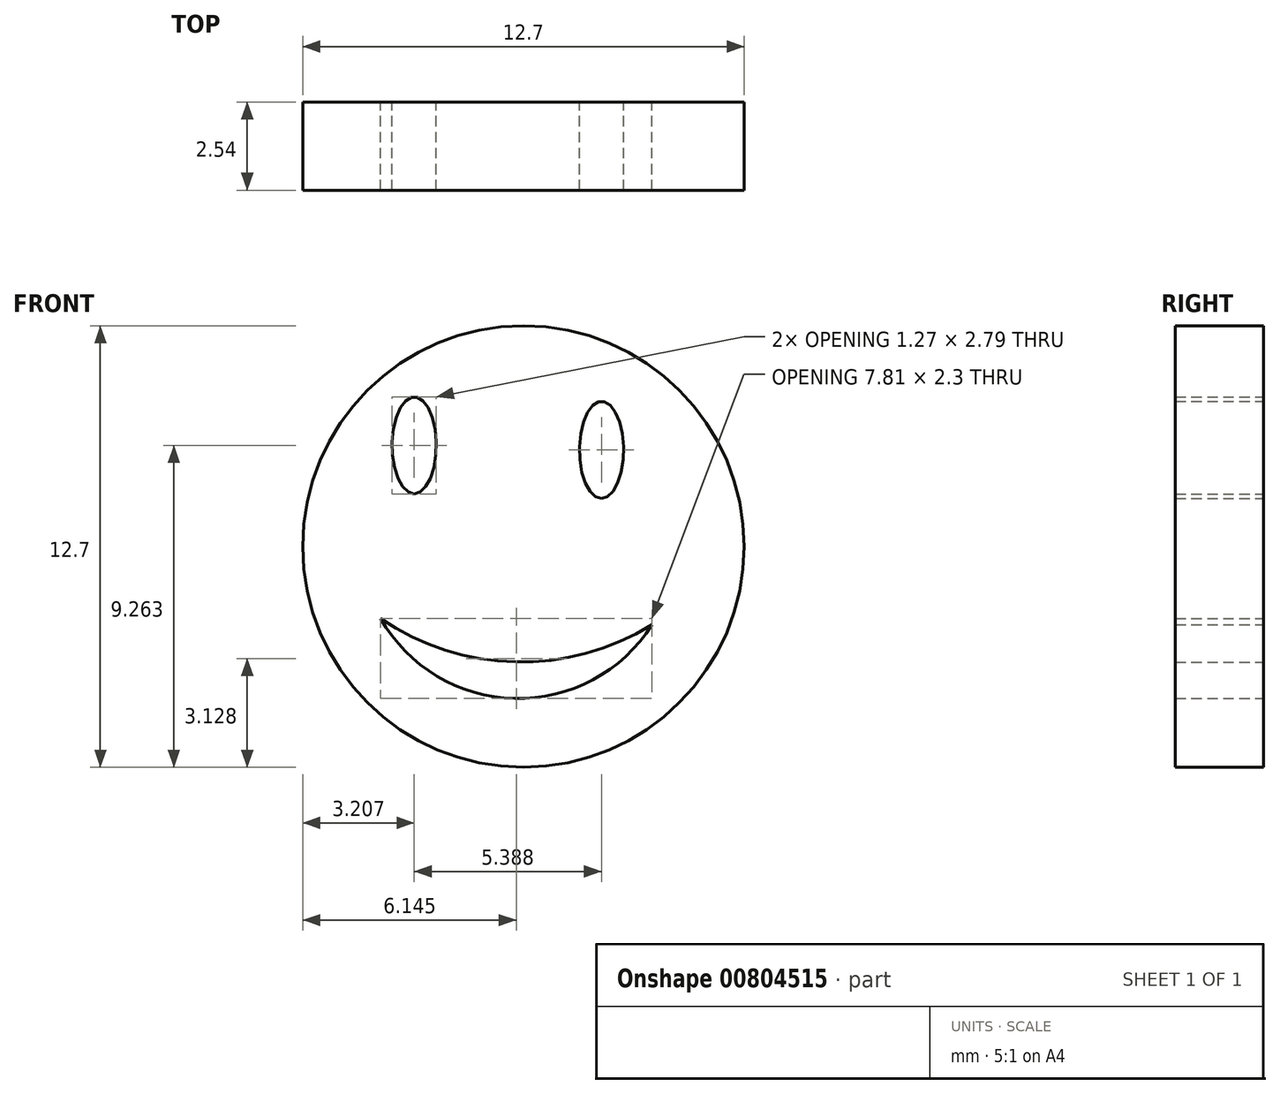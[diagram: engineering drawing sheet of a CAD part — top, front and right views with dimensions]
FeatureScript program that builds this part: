
annotation { "Feature Type Name" : "Feature", "Feature Type Description" : "" }
export const myFeature = defineFeature(function(context is Context, id is Id, definition is map)
    precondition{}
    {
        {
            var Q0;
            Q0=qCreatedBy(makeId("Front.planeOp"),FACE);
            var sketch = newSketch(context, id + "F0", { "sketchPlane" : qUnion([Q0])});
            skCircle(sketch, "E0", {"center": v(0, 0) * mm, "radius": 6.35 * mm, "construction": true});
            skCircle(sketch, "E1", {"center": v(0, 0) * mm, "radius": 6.35 * mm});
            skEllipse(sketch, "E2", {"center": v(-3.14, 2.91) * mm, "majorRadius": 1.4 * mm, "minorRadius": 0.64 * mm, "majorAxis": v(0, -1)});
            skEllipse(sketch, "E3", {"center": v(2.25, 2.78) * mm, "majorRadius": 1.4 * mm, "minorRadius": 0.64 * mm, "majorAxis": v(0, -1)});
            skArc(sketch, "E4", {"start": v(-4.11, -2.07) * mm, "mid": v(-0.26, -4.37) * mm, "end": v(3.7, -2.25) * mm});
            skArc(sketch, "E5", {"start": v(-4.11, -2.07) * mm, "mid": v(-0.23, -3.32) * mm, "end": v(3.7, -2.25) * mm});
            skSolve(sketch);
        }
        {
            var Q0;
            Q0 = qSketchRegion(id + "F0", true);
            extrude(context, id + "F1", {"entities" : qUnion([Q0]), "depth" : 2.54 * mm, "offsetDistance" : 25.4 * mm});
        }
    });
